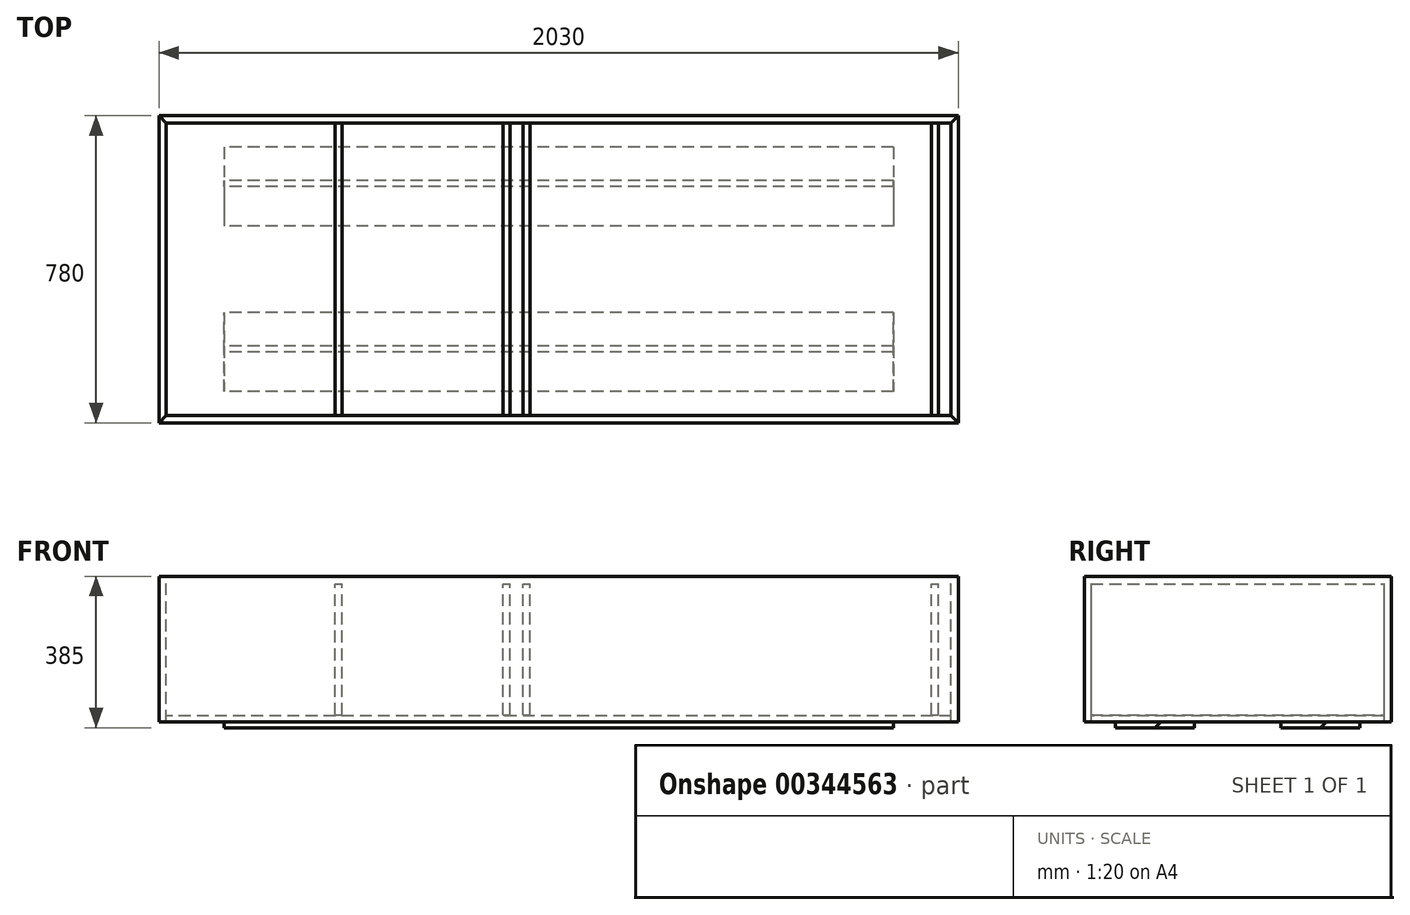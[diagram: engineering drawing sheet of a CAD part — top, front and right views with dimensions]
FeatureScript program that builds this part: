
annotation { "Feature Type Name" : "Feature", "Feature Type Description" : "" }
export const myFeature = defineFeature(function(context is Context, id is Id, definition is map)
    precondition{}
    {
        {
            assignVariable(context, id + "F0", {"name" : "WD", "anyValue" : 18});
        }
        {
            assignVariable(context, id + "F1", {"name" : "Diepte", "anyValue" : 370});
        }
        {
            var Q0;
            Q0=qCreatedBy(makeId("Top.planeOp"),FACE);
            var sketch = newSketch(context, id + "F2", { "sketchPlane" : qUnion([Q0])});
            skLineSegment(sketch, "E0.bottom", {"start": v(-1015, 390) * mm, "end": v(1015, 390) * mm});
            skLineSegment(sketch, "E0.top", {"start": v(-1015, -390) * mm, "end": v(1015, -390) * mm});
            skLineSegment(sketch, "E0.left", {"start": v(-1015, 390) * mm, "end": v(-1015, -390) * mm});
            skLineSegment(sketch, "E0.right", {"start": v(1015, 390) * mm, "end": v(1015, -390) * mm});
            skPoint(sketch, "E0.middle", {"position": v(0, 0) * mm});
            skLineSegment(sketch, "E1.0", {"start": v(-997, 372) * mm, "end": v(997, 372) * mm});
            skLineSegment(sketch, "E1.1", {"start": v(-997, 372) * mm, "end": v(-997, -372) * mm});
            skLineSegment(sketch, "E1.2", {"start": v(-997, -372) * mm, "end": v(997, -372) * mm});
            skLineSegment(sketch, "E1.3", {"start": v(997, 372) * mm, "end": v(997, -372) * mm});
            skLineSegment(sketch, "E2", {"start": v(-559, -390) * mm, "end": v(-559, 390) * mm, "construction": true});
            skLineSegment(sketch, "E3", {"start": v(-568, -372) * mm, "end": v(-568, 372) * mm});
            skLineSegment(sketch, "E4.MirrorCS", {"start": v(-550, -372) * mm, "end": v(-550, 372) * mm});
            skLineSegment(sketch, "E5", {"start": v(-132, -372) * mm, "end": v(-132, 372) * mm, "construction": true});
            skLineSegment(sketch, "E6", {"start": v(-141, -372) * mm, "end": v(-141, 372) * mm});
            skLineSegment(sketch, "E7.MirrorCS", {"start": v(-123, -372) * mm, "end": v(-123, 372) * mm});
            skLineSegment(sketch, "E8", {"start": v(965, -372) * mm, "end": v(965, 372) * mm});
            skLineSegment(sketch, "E9", {"start": v(947, -372) * mm, "end": v(947, 372) * mm});
            skLineSegment(sketch, "E10", {"start": v(-123, 372) * mm, "end": v(997, -372) * mm, "construction": true});
            skLineSegment(sketch, "E11", {"start": v(437, 0) * mm, "end": v(437, 218.87) * mm, "construction": true});
            skLineSegment(sketch, "E12.MirrorCS", {"start": v(-73, -372) * mm, "end": v(-73, 372) * mm});
            skLineSegment(sketch, "E13.MirrorCS", {"start": v(-91, -372) * mm, "end": v(-91, 372) * mm});
            skLineSegment(sketch, "E14", {"start": v(-1015, -390) * mm, "end": v(-997, -372) * mm});
            skLineSegment(sketch, "E15", {"start": v(-997, 372) * mm, "end": v(-1015, 390) * mm});
            skLineSegment(sketch, "E16", {"start": v(997, 372) * mm, "end": v(1015, 390) * mm});
            skLineSegment(sketch, "E17", {"start": v(997, -372) * mm, "end": v(1015, -390) * mm});
            skSolve(sketch);
        }
        {
            var Q0;
            Q0=sQuery(id+"F2.wireOp",EDGE,"E0.top");
            cPlane(context, id + "F3", {"entities" : qUnion([Q0]), "cplaneType" : CPlaneType.LINE_ANGLE, "offset" : 25 * mm, "angle" : 0 * degree, "width" : 150 * mm, "height" : 150 * mm});
        }
        {
            var Q0;
            Q0=qCreatedBy(id+"F3.planeOp",FACE);
            var sketch = newSketch(context, id + "F4", { "sketchPlane" : qUnion([Q0])});
            skLineSegment(sketch, "E18.0", {"start": v(1015, 0) * mm, "end": v(-1015, 0) * mm});
            skLineSegment(sketch, "E19", {"start": v(1015, 0) * mm, "end": v(1015, -370) * mm});
            skLineSegment(sketch, "E20", {"start": v(1015, -370) * mm, "end": v(-1015, -370) * mm});
            skLineSegment(sketch, "E21", {"start": v(-1015, -370) * mm, "end": v(-1015, 0) * mm});
            skLineSegment(sketch, "E22", {"start": v(-1015, -355) * mm, "end": v(1015, -355) * mm});
            skLineSegment(sketch, "E23", {"start": v(997, -370) * mm, "end": v(997, -355) * mm});
            skLineSegment(sketch, "E24", {"start": v(-997, -370) * mm, "end": v(-997, -355) * mm});
            skSolve(sketch);
        }
        {
            var Q0;
            Q0=qCreatedBy(makeId("Top.planeOp"),FACE);
            cPlane(context, id + "F5", {"entities" : qUnion([Q0]), "cplaneType" : CPlaneType.OFFSET, "offset" : 20 * mm, "oppositeDirection" : true, "width" : 150 * mm, "height" : 150 * mm});
        }
        {
            var Q0;
            Q0=qCreatedBy(id+"F5.planeOp",FACE);
            var sketch = newSketch(context, id + "F6", { "sketchPlane" : qUnion([Q0])});
            skLineSegment(sketch, "E25.0", {"start": v(-550, -372) * mm, "end": v(-550, 372) * mm});
            skLineSegment(sketch, "E25.1", {"start": v(-568, -372) * mm, "end": v(-568, 372) * mm});
            skLineSegment(sketch, "E25.2", {"start": v(-997, -372) * mm, "end": v(997, -372) * mm});
            skLineSegment(sketch, "E25.3", {"start": v(-141, -372) * mm, "end": v(-141, 372) * mm});
            skLineSegment(sketch, "E25.4", {"start": v(-123, -372) * mm, "end": v(-123, 372) * mm});
            skLineSegment(sketch, "E25.5", {"start": v(-91, -372) * mm, "end": v(-91, 372) * mm});
            skLineSegment(sketch, "E25.6", {"start": v(-73, -372) * mm, "end": v(-73, 372) * mm});
            skLineSegment(sketch, "E25.7", {"start": v(965, -372) * mm, "end": v(965, 372) * mm});
            skLineSegment(sketch, "E25.8", {"start": v(947, -372) * mm, "end": v(947, 372) * mm});
            skLineSegment(sketch, "E26.0", {"start": v(-997, 372) * mm, "end": v(997, 372) * mm});
            skSolve(sketch);
        }
        {
            var Q0;
            Q0=qCreatedBy(id+"F3.planeOp",FACE);
            cPlane(context, id + "F7", {"entities" : qUnion([Q0]), "cplaneType" : CPlaneType.OFFSET, "offset" : (getVariable(context, 'WD')) * mm, "width" : 150 * mm, "height" : 150 * mm});
        }
        {
            var Q0;
            Q0=qCreatedBy(id+"F7.planeOp",FACE);
            var sketch = newSketch(context, id + "F8", { "sketchPlane" : qUnion([Q0])});
            skLineSegment(sketch, "E27.0", {"start": v(1015, -370) * mm, "end": v(-1015, -370) * mm});
            skLineSegment(sketch, "E28.0", {"start": v(1015, 0) * mm, "end": v(1015, -370) * mm});
            skLineSegment(sketch, "E29.0", {"start": v(-1015, -355) * mm, "end": v(1015, -355) * mm});
            skLineSegment(sketch, "E30.0", {"start": v(-1015, -370) * mm, "end": v(-1015, 0) * mm});
            skLineSegment(sketch, "E31.0", {"start": v(997, -370) * mm, "end": v(997, -355) * mm});
            skLineSegment(sketch, "E32.0", {"start": v(-997, -370) * mm, "end": v(-997, -355) * mm});
            skSolve(sketch);
        }
        {
            var Q0;
            Q0=sQuery(id+"F4.wireOp",EDGE,"E20");
            cPlane(context, id + "F9", {"entities" : qUnion([Q0]), "cplaneType" : CPlaneType.LINE_ANGLE, "offset" : 25 * mm, "angle" : 90 * degree, "width" : 150 * mm, "height" : 150 * mm});
        }
        {
            var Q0;
            Q0=qCreatedBy(id+"F9.planeOp",FACE);
            var sketch = newSketch(context, id + "F10", { "sketchPlane" : qUnion([Q0])});
            skLineSegment(sketch, "E33.0", {"start": v(-1015, -390) * mm, "end": v(1015, -390) * mm});
            skLineSegment(sketch, "E34", {"start": v(1015, -390) * mm, "end": v(1015, 390) * mm});
            skLineSegment(sketch, "E35", {"start": v(1015, 390) * mm, "end": v(-1015, 390) * mm});
            skLineSegment(sketch, "E36", {"start": v(-1015, 390) * mm, "end": v(-1015, -390) * mm});
            skLineSegment(sketch, "E37", {"start": v(1015, -390) * mm, "end": v(-1015, 390) * mm, "construction": true});
            skLineSegment(sketch, "E38", {"start": v(0, 0) * mm, "end": v(0, 390) * mm, "construction": true});
            skSolve(sketch);
        }
        {
            var Q0;
            Q0=sQuery(id+"F10.wireOp",EDGE,"E38");
            cPlane(context, id + "F11", {"entities" : qUnion([Q0]), "cplaneType" : CPlaneType.LINE_ANGLE, "offset" : 25 * mm, "angle" : 90 * degree, "width" : 150 * mm, "height" : 150 * mm});
        }
        {
            var Q0;
            Q0=qCreatedBy(id+"F11.planeOp",FACE);
            var sketch = newSketch(context, id + "F12", { "sketchPlane" : qUnion([Q0])});
            skLineSegment(sketch, "E39.0", {"start": v(390, -370) * mm, "end": v(-390, -370) * mm});
            skLineSegment(sketch, "E40", {"start": v(310, -370) * mm, "end": v(310, -385) * mm});
            skLineSegment(sketch, "E41", {"start": v(310, -385) * mm, "end": v(210, -385) * mm});
            skLineSegment(sketch, "E42", {"start": v(210, -385) * mm, "end": v(210, -370) * mm, "construction": true});
            skLineSegment(sketch, "E43", {"start": v(210, -385) * mm, "end": v(110, -385) * mm});
            skLineSegment(sketch, "E44", {"start": v(110, -385) * mm, "end": v(110, -370) * mm});
            skLineSegment(sketch, "E45", {"start": v(0, -370) * mm, "end": v(0, -555.2) * mm, "construction": true});
            skPoint(sketch, "E45.endSnap0", {"position": v(0, -370) * mm});
            skLineSegment(sketch, "E46.MirrorCS", {"start": v(-110, -385) * mm, "end": v(-110, -370) * mm});
            skLineSegment(sketch, "E47.MirrorCS", {"start": v(-210, -385) * mm, "end": v(-110, -385) * mm});
            skLineSegment(sketch, "E48.MirrorCS", {"start": v(-310, -385) * mm, "end": v(-210, -385) * mm});
            skLineSegment(sketch, "E49.MirrorCS", {"start": v(-310, -370) * mm, "end": v(-310, -385) * mm});
            skLineSegment(sketch, "E50.MirrorCS", {"start": v(-210, -385) * mm, "end": v(-210, -370) * mm, "construction": true});
            skLineSegment(sketch, "E51", {"start": v(210, -385) * mm, "end": v(225, -370) * mm});
            skLineSegment(sketch, "E52", {"start": v(-210, -385) * mm, "end": v(-195, -370) * mm});
            skSolve(sketch);
        }
        {
            var Q0;
            {var subQ0=sQuery(id+"F6.wireOp",EDGE,"E25.7");Q0=makeQuery(id+"F6.imprint","IMPRINT",FACE,{"disambiguationData":[TD([[makeQuery(id+"F6.imprint","IMPRINT",EDGE,{"derivedFrom":subQ0}),1.0]])]});}
            var Q1;
            {var subQ0=sQuery(id+"F6.wireOp",EDGE,"E25.5");Q1=makeQuery(id+"F6.imprint","IMPRINT",FACE,{"disambiguationData":[TD([[makeQuery(id+"F6.imprint","IMPRINT",EDGE,{"derivedFrom":subQ0}),-1.0]])]});}
            var Q2;
            {var subQ0=sQuery(id+"F6.wireOp",EDGE,"E25.3");Q2=makeQuery(id+"F6.imprint","IMPRINT",FACE,{"disambiguationData":[TD([[makeQuery(id+"F6.imprint","IMPRINT",EDGE,{"derivedFrom":subQ0}),-1.0]])]});}
            var Q3;
            {var subQ0=sQuery(id+"F6.wireOp",EDGE,"E25.0");Q3=makeQuery(id+"F6.imprint","IMPRINT",FACE,{"disambiguationData":[TD([[makeQuery(id+"F6.imprint","IMPRINT",EDGE,{"derivedFrom":subQ0}),1.0]])]});}
            extrude(context, id + "F13", {"entities" : qUnion([Q0, Q1, Q2, Q3]), "oppositeDirection" : true, "depth" : (getVariable(context, 'Diepte') - 20 - 18) * mm});
        }
        {
            var Q0;
            Q0=makeQuery(id+"F2.imprint","IMPRINT",FACE,{"disambiguationData":[TD([[makeQuery(id+"F2.imprint","IMPRINT",EDGE,{"derivedFrom":sQuery(id+"F2.wireOp",EDGE,"E0.left")}),1.0]])]});
            var Q1;
            Q1=makeQuery(id+"F2.imprint","IMPRINT",FACE,{"disambiguationData":[TD([[makeQuery(id+"F2.imprint","IMPRINT",EDGE,{"derivedFrom":sQuery(id+"F2.wireOp",EDGE,"E0.right")}),-1.0]])]});
            extrude(context, id + "F14", {"entities" : qUnion([Q0, Q1]), "oppositeDirection" : true, "depth" : (getVariable(context, 'Diepte')) * mm});
        }
        {
            var Q0;
            Q0=makeQuery(id+"F2.imprint","IMPRINT",FACE,{"disambiguationData":[TD([[makeQuery(id+"F2.imprint","IMPRINT",EDGE,{"derivedFrom":sQuery(id+"F2.wireOp",EDGE,"E0.bottom")}),-1.0]])]});
            var Q1;
            Q1=makeQuery(id+"F2.imprint","IMPRINT",FACE,{"disambiguationData":[TD([[makeQuery(id+"F2.imprint","IMPRINT",EDGE,{"derivedFrom":sQuery(id+"F2.wireOp",EDGE,"E0.top")}),1.0]])]});
            extrude(context, id + "F15", {"entities" : qUnion([Q0, Q1]), "oppositeDirection" : true, "depth" : (getVariable(context, 'Diepte')) * mm});
        }
        {
            var Q0;
            {var subQ3=sQuery(id+"F8.wireOp",EDGE,"E31.0");Q0=makeQuery(id+"F8.imprint","IMPRINT",FACE,{"disambiguationData":[TD([[makeQuery(id+"F8.imprint","IMPRINT",EDGE,{"derivedFrom":subQ3}),1.0]])]});}
            extrude(context, id + "F16", {"entities" : qUnion([Q0]), "depth" : (780 - 18 - 18) * mm});
        }
        {
            var Q0;
            {var subQ0=sQuery(id+"F12.wireOp",EDGE,"E40");Q0=makeQuery(id+"F12.imprint","IMPRINT",FACE,{"disambiguationData":[TD([[makeQuery(id+"F12.imprint","IMPRINT",EDGE,{"derivedFrom":subQ0}),-1.0]])]});}
            var Q1;
            {var subQ0=sQuery(id+"F12.wireOp",EDGE,"E46.MirrorCS");Q1=makeQuery(id+"F12.imprint","IMPRINT",FACE,{"disambiguationData":[TD([[makeQuery(id+"F12.imprint","IMPRINT",EDGE,{"derivedFrom":subQ0}),1.0]])]});}
            extrude(context, id + "F17", {"entities" : qUnion([Q0, Q1]), "depth" : 850 * mm, "hasSecondDirection" : true, "secondDirectionOppositeDirection" : true, "secondDirectionDepth" : 850 * mm});
        }
        {
            var Q0;
            Q0=makeQuery(id+"F12.imprint","IMPRINT",FACE,{"disambiguationData":[TD([[makeQuery(id+"F12.imprint","IMPRINT",EDGE,{"derivedFrom":sQuery(id+"F12.wireOp",EDGE,"E48.MirrorCS")}),1.0]])]});
            var Q1;
            Q1=makeQuery(id+"F12.imprint","IMPRINT",FACE,{"disambiguationData":[TD([[makeQuery(id+"F12.imprint","IMPRINT",EDGE,{"derivedFrom":sQuery(id+"F12.wireOp",EDGE,"E43")}),-1.0]])]});
            extrude(context, id + "F18", {"entities" : qUnion([Q0, Q1]), "depth" : 850 * mm, "hasSecondDirection" : true, "secondDirectionOppositeDirection" : true, "secondDirectionDepth" : 850 * mm});
        }
    });
